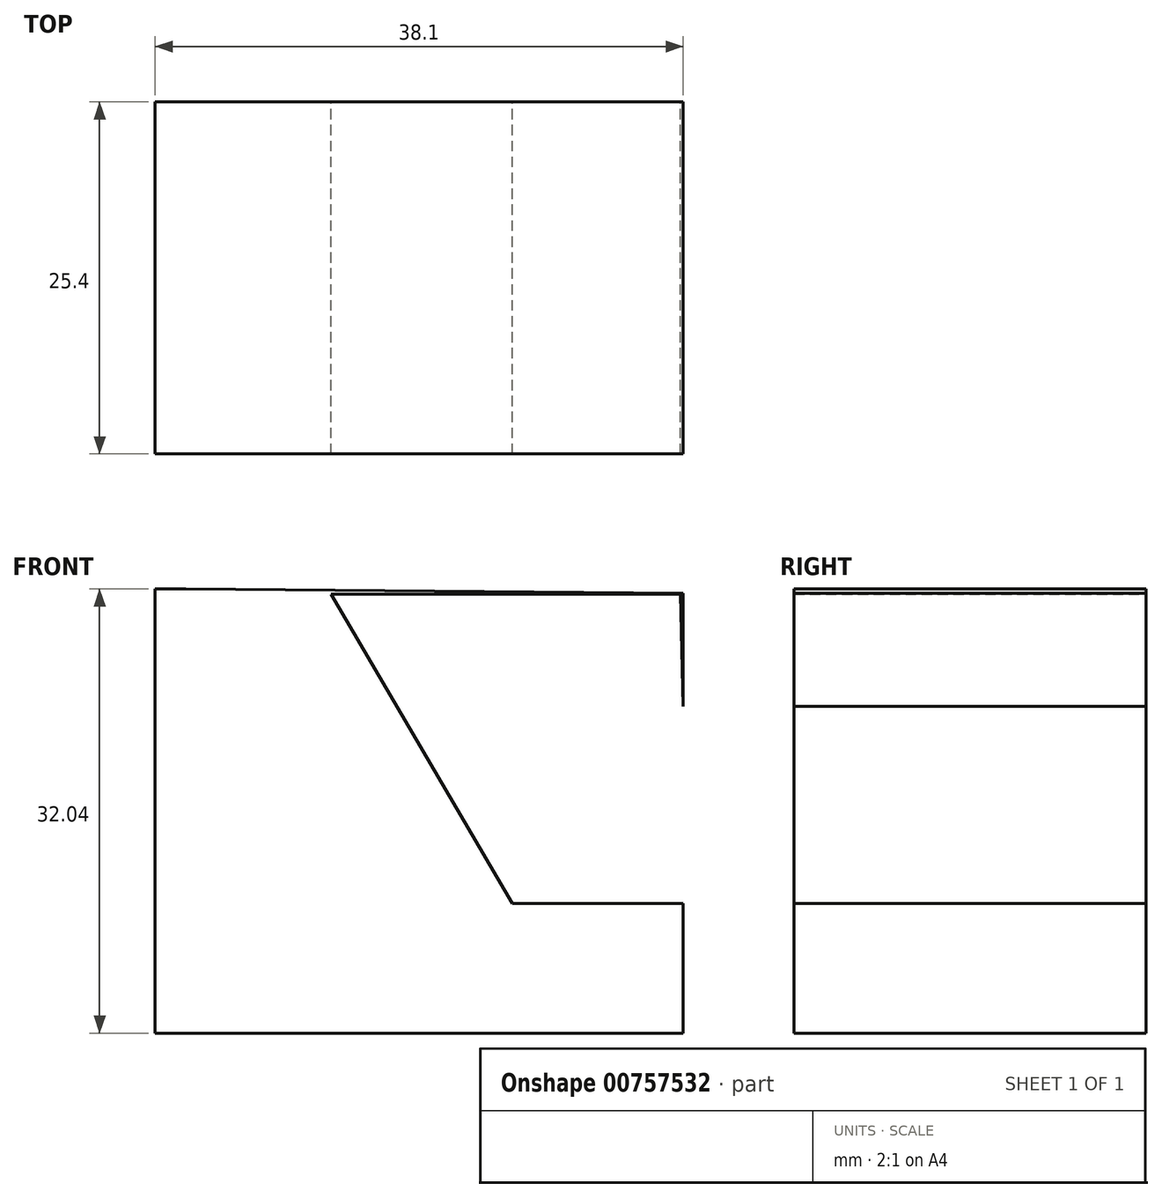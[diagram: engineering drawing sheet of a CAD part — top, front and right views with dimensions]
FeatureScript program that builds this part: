
annotation { "Feature Type Name" : "Feature", "Feature Type Description" : "" }
export const myFeature = defineFeature(function(context is Context, id is Id, definition is map)
    precondition{}
    {
        {
            var Q0;
            Q0=qCreatedBy(makeId("Front.planeOp"),FACE);
            var sketch = newSketch(context, id + "F0", { "sketchPlane" : qUnion([Q0])});
            skLineSegment(sketch, "E0", {"start": v(0, 32.04) * mm, "end": v(0, 0) * mm});
            skLineSegment(sketch, "E1", {"start": v(0, 0) * mm, "end": v(38.1, 0) * mm});
            skLineSegment(sketch, "E2", {"start": v(38.1, 0) * mm, "end": v(38.1, 31.75) * mm});
            skLineSegment(sketch, "E3", {"start": v(2.2, 32.04) * mm, "end": v(38.1, 31.75) * mm});
            skLineSegment(sketch, "E4", {"start": v(2.2, 32.04) * mm, "end": v(0, 32.04) * mm});
            skSolve(sketch);
        }
        {
            var Q0;
            Q0 = qSketchRegion(id + "F0", true);
            extrude(context, id + "F1", {"entities" : qUnion([Q0]), "depth" : 25.4 * mm, "offsetDistance" : 25.4 * mm});
        }
        {
            var Q0;
            Q0=qCreatedBy(makeId("Front.planeOp"),FACE);
            var sketch = newSketch(context, id + "F2", { "sketchPlane" : qUnion([Q0])});
            skLineSegment(sketch, "E5", {"start": v(38.47, 9.35) * mm, "end": v(25.77, 9.35) * mm});
            skLineSegment(sketch, "E6", {"start": v(25.77, 9.35) * mm, "end": v(12.7, 31.66) * mm});
            skLineSegment(sketch, "E7", {"start": v(12.7, 31.66) * mm, "end": v(37.9, 31.66) * mm});
            skLineSegment(sketch, "E8", {"start": v(37.9, 31.66) * mm, "end": v(38.47, 9.35) * mm});
            skSolve(sketch);
        }
        {
            var Q0;
            Q0 = qSketchRegion(id + "F2", true);
            extrude(context, id + "F3", {"entities" : qUnion([Q0]), "operationType" : NewBodyOperationType.REMOVE, "endBound" : BoundingType.THROUGH_ALL, "depth" : 25.4 * mm, "offsetDistance" : 25.4 * mm});
        }
    });
